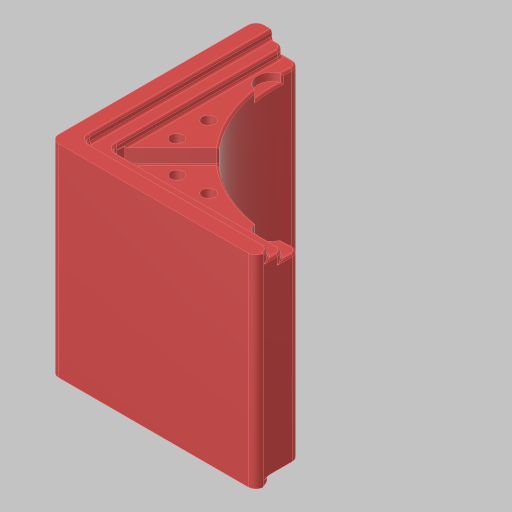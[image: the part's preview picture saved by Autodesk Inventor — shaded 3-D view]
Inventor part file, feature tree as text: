
AUTODESK INVENTOR PART (.ipt)
format: ipt  version: 2023.5 (Build 275446000, 446)  size: 464,384 bytes
history: native  units: in
note: dims shown in document units (in); Inventor stores cm internally (conversion verified against a paired STEP export)
features: extrude x9, sketch x8, projected_geometry x8, fillet x2, hole x1
ambient origin geometry x8: Origin, YZ Plane, XZ Plane, XY Plane, X Axis, Y Axis, Z Axis, Center Point
bodies: Solid1 (feature_tree)
feature tree (28):
  sketch  "Sketch1"  dims[d0=1.0in d1=1.0in]
  extrude  "Extrusion1"  Depth=1.0in
  hole  "Hole1"  [1 undecoded]
  extrude  "Extrusion2"  Depth=0.5in
  extrude  "Extrusion3"  Depth=2.125in
  extrude  "Extrusion4"  Depth=0.25in
  fillet  "Fillet1"  Radius=0.25in
  extrude  "Extrusion5"  Depth=0.3937in
  sketch  "Sketch6"  dims[d12=1.9685in d14=0.5in d15=0.3937in d17=1.0in d19=1.9685in d21=0.5in d22=0.3937in d24=1.0in]
  extrude  "Extrusion6"  Depth=0.0312in
  extrude  "Extrusion7"  Depth=0.0312in
  extrude  "Extrusion8"  Depth=0.0312in TaperAngle=0.0deg
  fillet  "Fillet2"  Radius=0.249in
  extrude  "Extrusion9"  Depth=0.0312in
  sketch  "Sketch2"  dims[d2=3.0in d3=3.0in]
  sketch  "Sketch3"  dims[d4=4.375in d5=0.5in]
  sketch  "Sketch4"  dims[d6=0.5in d7=2.125in]
  sketch  "Sketch5"  dims[d9=2.125in d10=0.25in d11=0.25in]
  projected_geometry  "Projected Loop1"
  projected_geometry  "Projected Loop2"
  projected_geometry  "Projected Loop3"
  sketch  "Sketch7"  dims[d26=2.837in d27=0.0in]
  sketch  "Sketch8"  dims[d28=0.201in d29=0.75in d30=0.563in d31=0.12in d32=0.5635in d33=0.2362in d34=0.0in d35=0.375in d36=0.1in d37=0.12in d38=0.0in d39=0.249in d40=0.249in d41=0.124in d42=0.0in d43=0.249in d44=0.249in d45=0.124in d46=0.0in d47=0.125in d48=0.35in d49=0.25in d50=0.0in d51=0.0312in d52=0.25in d53=0.0in d54=1.0in d55=0.0in d56=0.45in d57=0.45in d58=0.125in d59=0.0in d60=0.5in d61=0.5in d62=0.5in d63=0.125in d64=0.0in]
  projected_geometry  "Projected Loop4"
  projected_geometry  "Project Cut Edges1"
  projected_geometry  "Project Cut Edges2"
  projected_geometry  "Project Cut Edges3"
  projected_geometry  "Project Cut Edges4"
note: 1 required parameter value undecoded (feature->parameter linkage not recoverable at this tier; creation-order binding heuristic only, values carry confidence <= 0.55)
